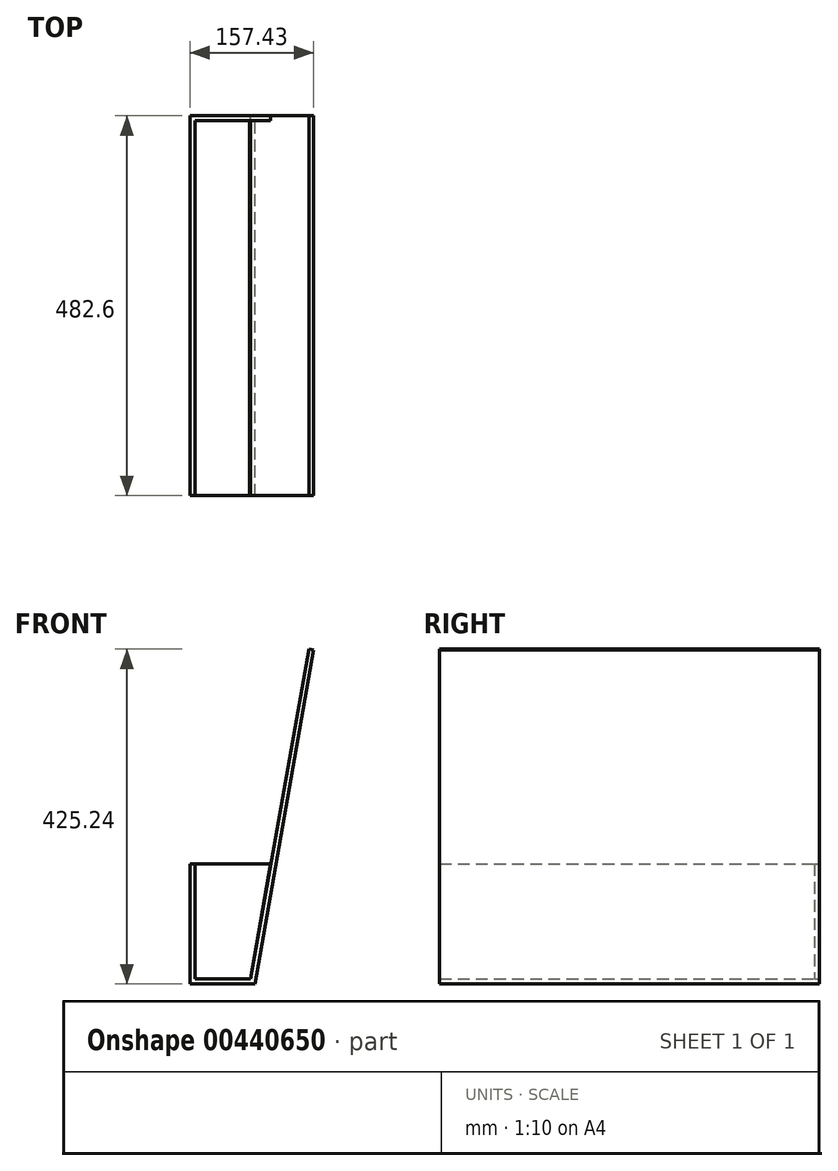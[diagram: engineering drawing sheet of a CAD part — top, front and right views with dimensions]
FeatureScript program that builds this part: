
annotation { "Feature Type Name" : "Feature", "Feature Type Description" : "" }
export const myFeature = defineFeature(function(context is Context, id is Id, definition is map)
    precondition{}
    {
        {
            var Q0;
            Q0=qCreatedBy(makeId("Front.planeOp"),FACE);
            var sketch = newSketch(context, id + "F0", { "sketchPlane" : qUnion([Q0])});
            skLineSegment(sketch, "E0", {"start": v(0, 0) * mm, "end": v(74.98, 425.24) * mm});
            skLineSegment(sketch, "E1", {"start": v(74.98, 425.24) * mm, "end": v(81.23, 424.14) * mm});
            skLineSegment(sketch, "E2", {"start": v(0, 0) * mm, "end": v(-76.2, 0) * mm});
            skLineSegment(sketch, "E3", {"start": v(81.23, 424.14) * mm, "end": v(6.45, 0) * mm});
            skLineSegment(sketch, "E4", {"start": v(6.45, 0) * mm, "end": v(0, 0) * mm});
            skLineSegment(sketch, "E5", {"start": v(-76.2, 0) * mm, "end": v(-76.2, 152.4) * mm});
            skLineSegment(sketch, "E6", {"start": v(-76.2, 152.4) * mm, "end": v(-69.85, 152.4) * mm});
            skLineSegment(sketch, "E7", {"start": v(-69.85, 152.4) * mm, "end": v(-69.85, 0) * mm});
            skLineSegment(sketch, "E8", {"start": v(-69.85, 0) * mm, "end": v(-69.85, 6.35) * mm});
            skLineSegment(sketch, "E9", {"start": v(-69.85, 6.35) * mm, "end": v(0, 6.35) * mm});
            skLineSegment(sketch, "E10", {"start": v(0, 6.35) * mm, "end": v(7.34, 5.06) * mm});
            skLineSegment(sketch, "E11", {"start": v(7.34, 5.06) * mm, "end": v(6.45, 0) * mm});
            skSolve(sketch);
        }
        {
            var Q0;
            Q0 = qSketchRegion(id + "F0", true);
            extrude(context, id + "F1", {"entities" : qUnion([Q0]), "depth" : 482.6 * mm});
        }
        {
            var Q0;
            Q0=qCreatedBy(makeId("Front.planeOp"),FACE);
            var sketch = newSketch(context, id + "F2", { "sketchPlane" : qUnion([Q0])});
            skLineSegment(sketch, "E12", {"start": v(0, 0) * mm, "end": v(-76.2, 0) * mm});
            skLineSegment(sketch, "E13", {"start": v(-76.2, 0) * mm, "end": v(-76.2, 152.4) * mm});
            skLineSegment(sketch, "E14", {"start": v(-76.2, 152.4) * mm, "end": v(26.4, 152.4) * mm});
            skLineSegment(sketch, "E15", {"start": v(26.4, 152.4) * mm, "end": v(0, 0) * mm});
            skSolve(sketch);
        }
        {
            var Q0;
            Q0 = qSketchRegion(id + "F2", true);
            extrude(context, id + "F3", {"entities" : qUnion([Q0]), "operationType" : NewBodyOperationType.ADD, "depth" : 6.35 * mm});
        }
    });
